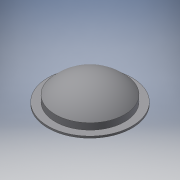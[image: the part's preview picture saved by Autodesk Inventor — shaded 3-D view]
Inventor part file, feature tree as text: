
AUTODESK INVENTOR PART (.ipt)
format: ipt  version: 2016 SP2 (Build 200236200, 236)  size: 138,752 bytes
history: native  units: mm
features: revolve x1, sketch x1, reference x1
ambient origin geometry x8: Origin, YZ Plane, XZ Plane, XY Plane, X Axis, Y Axis, Z Axis, Center Point
bodies: Volumenkörper1 (feature_tree)
feature tree (3):
  revolve  "Umdrehung1"
  sketch  "Skizze1"  dims[d0=2.0mm d1=7.0mm d2=8.0mm d3=46.0mm d4=0.5mm d5=0.5mm d7=50.0mm d8=9.0mm d9=4.0mm d10=42.760567mm]
  reference  "Referenz1"
